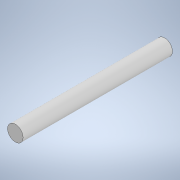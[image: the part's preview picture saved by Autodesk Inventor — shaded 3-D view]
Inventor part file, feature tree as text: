
AUTODESK INVENTOR PART (.ipt)
format: ipt  version: 2022 (Build 260153000, 153)  size: 96,768 bytes
history: native  units: mm
features: other x2, plane x1, extrude x1, sketch x1, reference x1
ambient origin geometry x8: Origin, YZ Plane, XZ Plane, XY Plane, X Axis, Y Axis, Z Axis, Center Point
bodies: Solid1 (feature_tree)
feature tree (6):
  plane  "Work Plane1"
  extrude  "Extrusion1"  [1 undecoded]
  sketch  "Sketch1"  dims[d0=12.0mm d1=0.0mm]
  reference  "Reference1"
  other  "Caja_Reductora_.iam"
  other  "Eje_Salida:1"
note: 1 required parameter value undecoded (feature->parameter linkage not recoverable at this tier; creation-order binding heuristic only, values carry confidence <= 0.55)
